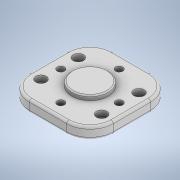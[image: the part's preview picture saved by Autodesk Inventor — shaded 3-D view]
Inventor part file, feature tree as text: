
AUTODESK INVENTOR PART (.ipt)
format: ipt  version: 2020 (Build 240168000, 168)  size: 224,768 bytes
history: native  units: in
note: dims shown in document units (in); Inventor stores cm internally (conversion verified against a paired STEP export)
features: sketch x5, extrude x3, hole x2, fillet x2, pattern_linear x1, pattern_circular x1, chamfer x1
ambient origin geometry x8: Origin, YZ Plane, XZ Plane, XY Plane, X Axis, Y Axis, Z Axis, Center Point
bodies: Solid1 (feature_tree)
feature tree (15):
  extrude  "Extrusion1"  Depth=2.8346in
  hole  "Hole1"  [1 undecoded]
  pattern_linear  "Rectangular Pattern1"  Count1=2 Spacing1=2.0472in
  hole  "Hole2"  [1 undecoded]
  extrude  "Extrusion3"  Depth=0.3937in
  pattern_circular  "Circular Pattern3"  [2 undecoded]
  extrude  "Extrusion4"  Depth=1.5748in TaperAngle=360.0deg
  chamfer  "Chamfer1"  Distance=1.2205in
  fillet  "Fillet1"  Radius=0.1575in
  fillet  "Fillet2"  Radius=0.0787in
  sketch  "Sketch1"  dims[d2=0.3937in d3=0.0in d4=2.8346in]
  sketch  "Sketch2"  dims[d5=2.8346in]
  sketch  "Sketch3"  dims[d6=0.2165in d7=0.2362in d8=0.3543in d9=0.1969in d10=90.0deg d11=0.315in d12=0.8108in d13=0.6299in]
  sketch  "Sketch5"  dims[d14=1.0236in d15=0.7874in d17=2.0472in d18=0.7874in d20=1.2598in]
  sketch  "Sketch6"  dims[d21=0.248in d22=0.2362in d23=0.4819in d24=0.1409in d25=90.0deg d26=0.315in d27=0.8108in d28=0.9843in d38=0.3937in d39=0.1969in d40=0.0in d41=1.5748in d42=360.0deg d44=1.2205in d45=0.1575in d46=0.0in d47=0.0394in d48=0.0787in d49=45.0deg d50=0.7874in d51=0.0787in]
note: 4 required parameter values undecoded (feature->parameter linkage not recoverable at this tier; creation-order binding heuristic only, values carry confidence <= 0.55)
